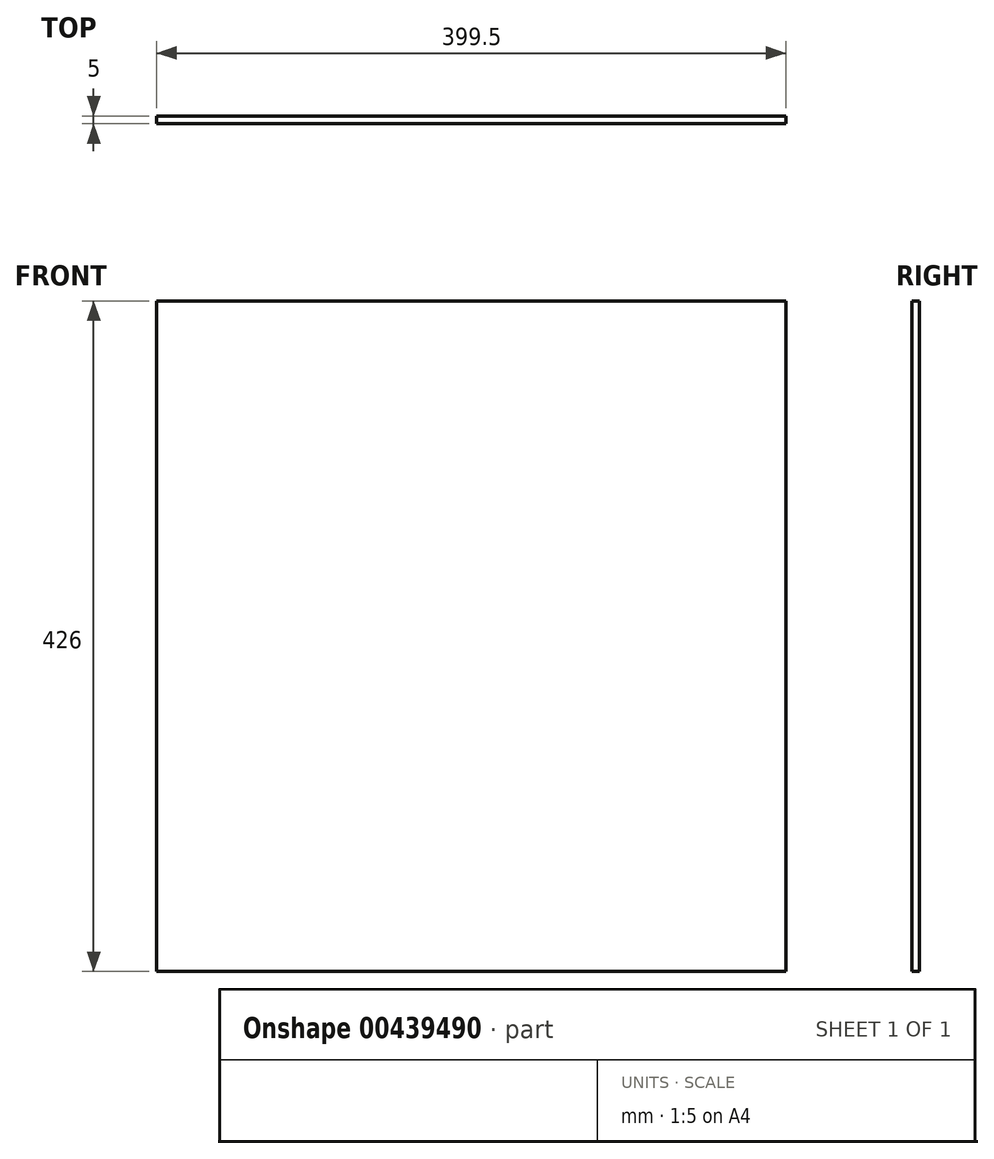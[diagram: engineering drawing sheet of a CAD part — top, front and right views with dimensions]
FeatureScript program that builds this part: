
annotation { "Feature Type Name" : "Feature", "Feature Type Description" : "" }
export const myFeature = defineFeature(function(context is Context, id is Id, definition is map)
    precondition{}
    {
        {
            var Q0;
            Q0=qCreatedBy(makeId("Front.planeOp"),FACE);
            var sketch = newSketch(context, id + "F0", { "sketchPlane" : qUnion([Q0])});
            skLineSegment(sketch, "E0.bottom", {"start": v(-199.75, 426) * mm, "end": v(199.75, 426) * mm});
            skLineSegment(sketch, "E0.top", {"start": v(-199.75, 0) * mm, "end": v(199.75, 0) * mm});
            skLineSegment(sketch, "E0.left", {"start": v(-199.75, 426) * mm, "end": v(-199.75, 0) * mm});
            skLineSegment(sketch, "E0.right", {"start": v(199.75, 426) * mm, "end": v(199.75, 0) * mm});
            skSolve(sketch);
        }
        {
            var Q0;
            Q0 = qSketchRegion(id + "F0", true);
            extrude(context, id + "F1", {"entities" : qUnion([Q0]), "depth" : 5 * mm, "offsetDistance" : 25 * mm});
        }
    });
